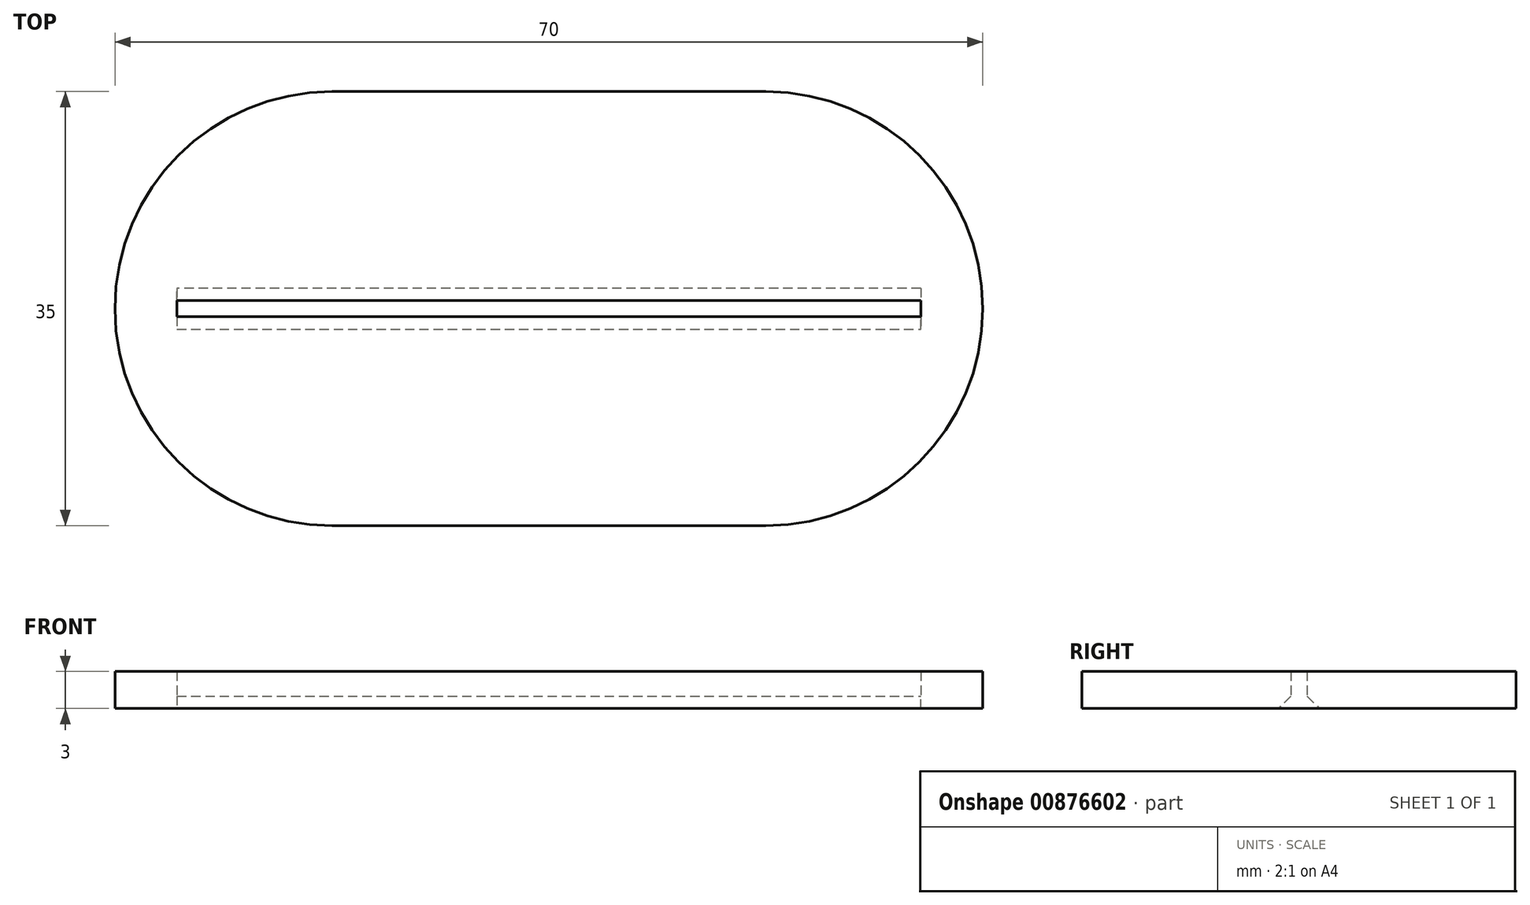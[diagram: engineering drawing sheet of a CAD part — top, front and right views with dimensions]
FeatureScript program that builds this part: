
annotation { "Feature Type Name" : "Feature", "Feature Type Description" : "" }
export const myFeature = defineFeature(function(context is Context, id is Id, definition is map)
    precondition{}
    {
        {
            var Q0;
            Q0=qCreatedBy(makeId("Top.planeOp"),FACE);
            var sketch = newSketch(context, id + "F0", { "sketchPlane" : qUnion([Q0])});
            skLineSegment(sketch, "E0.bottom", {"start": v(0, 0) * mm, "end": v(70, 0) * mm});
            skLineSegment(sketch, "E0.top", {"start": v(0, 35) * mm, "end": v(70, 35) * mm});
            skLineSegment(sketch, "E0.left", {"start": v(0, 0) * mm, "end": v(0, 35) * mm});
            skLineSegment(sketch, "E0.right", {"start": v(70, 0) * mm, "end": v(70, 35) * mm});
            skLineSegment(sketch, "E1.bottom", {"start": v(5, 18.15) * mm, "end": v(65, 18.15) * mm});
            skLineSegment(sketch, "E1.top", {"start": v(5, 16.85) * mm, "end": v(65, 16.85) * mm});
            skLineSegment(sketch, "E1.left", {"start": v(5, 18.15) * mm, "end": v(5, 16.85) * mm});
            skLineSegment(sketch, "E1.right", {"start": v(65, 18.15) * mm, "end": v(65, 16.85) * mm});
            skSolve(sketch);
        }
        {
            var Q0;
            Q0=qSketchRegion(id+"F0",true);
            extrude(context, id + "F1", {"entities" : qUnion([Q0]), "depth" : 3 * mm, "offsetDistance" : 25 * mm});
        }
        {
            var Q0;
            Q0=makeQuery(id+"F1.opExtrude","SWEPT_EDGE",EDGE,{"disambiguationData":[OSD([sQuery(id+"F0.wireOp",EDGE,"E0.bottom"),sQuery(id+"F0.wireOp",EDGE,"E0.right")])]});
            var Q1;
            Q1=makeQuery(id+"F1.opExtrude","SWEPT_EDGE",EDGE,{"disambiguationData":[OSD([sQuery(id+"F0.wireOp",EDGE,"E0.top"),sQuery(id+"F0.wireOp",EDGE,"E0.right")])]});
            var Q2;
            Q2=makeQuery(id+"F1.opExtrude","SWEPT_EDGE",EDGE,{"disambiguationData":[OSD([sQuery(id+"F0.wireOp",EDGE,"E0.top"),sQuery(id+"F0.wireOp",EDGE,"E0.left")])]});
            var Q3;
            Q3=makeQuery(id+"F1.opExtrude","SWEPT_EDGE",EDGE,{"disambiguationData":[OSD([sQuery(id+"F0.wireOp",EDGE,"E0.bottom"),sQuery(id+"F0.wireOp",EDGE,"E0.left")])]});
            fillet(context, id + "F2", {"entities" : qUnion([Q0, Q1, Q2, Q3]), "radius" : 17.5 * mm, "tangentPropagation" : true, "allowEdgeOverflow" : false});
        }
        {
            var Q0;
            Q0=makeQuery(id+"F1.opExtrude","CAP_EDGE",EDGE,{"disambiguationData":[OSD([sQuery(id+"F0.wireOp",EDGE,"E1.top")])],"isStart":true});
            var Q1;
            Q1=makeQuery(id+"F1.opExtrude","CAP_EDGE",EDGE,{"disambiguationData":[OSD([sQuery(id+"F0.wireOp",EDGE,"E1.bottom")])],"isStart":true});
            chamfer(context, id + "F3", {"entities" : qUnion([Q0, Q1]), "width" : 1 * mm, "tangentPropagation" : true});
        }
    });
